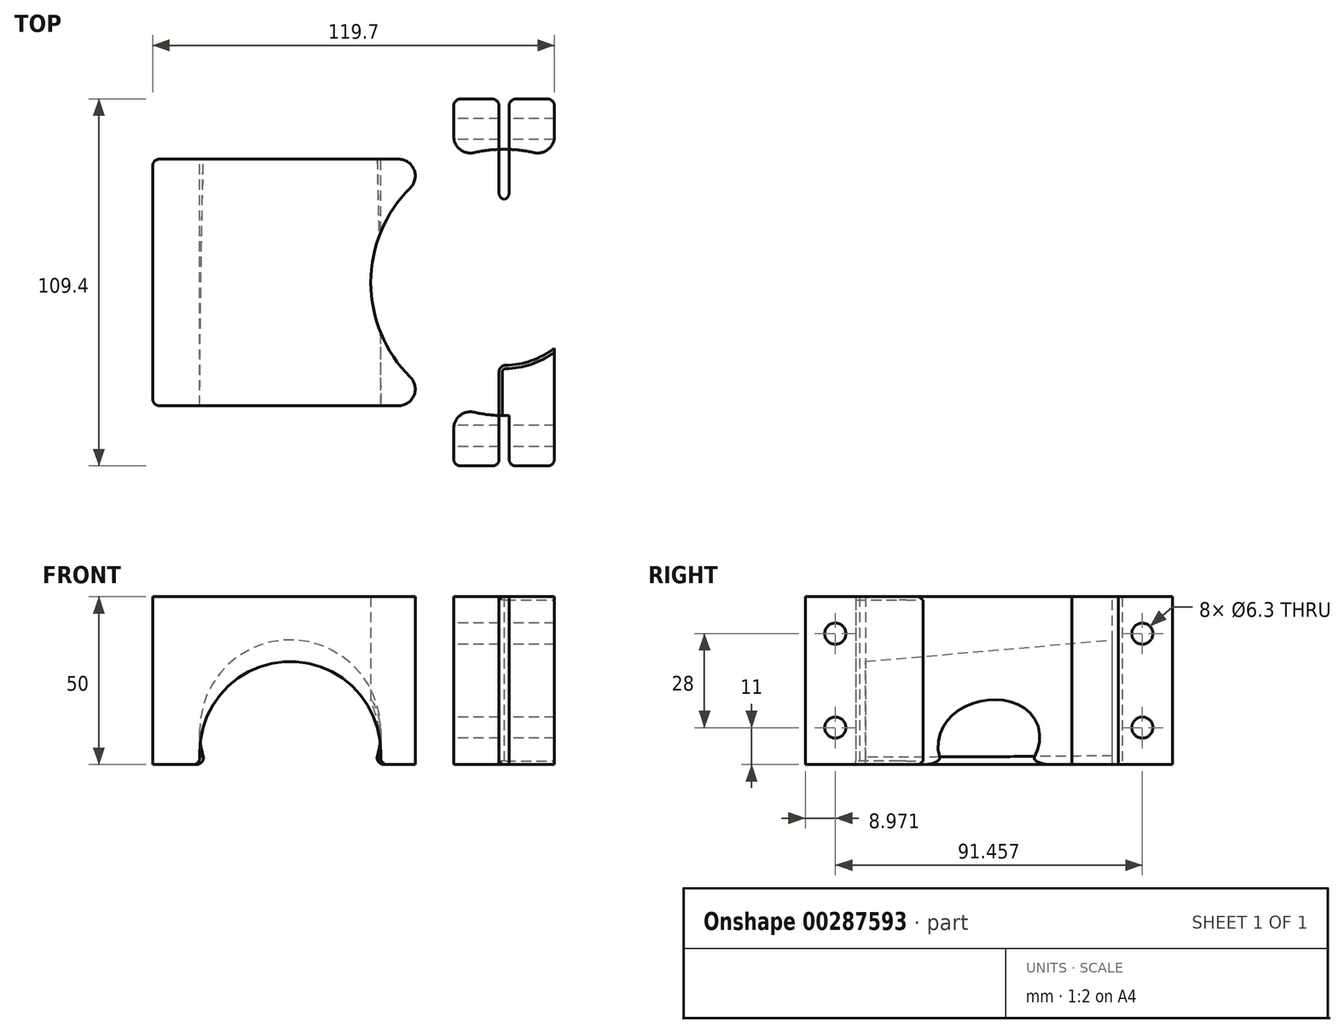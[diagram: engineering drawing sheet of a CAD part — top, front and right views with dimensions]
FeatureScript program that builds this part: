
annotation { "Feature Type Name" : "Feature", "Feature Type Description" : "" }
export const myFeature = defineFeature(function(context is Context, id is Id, definition is map)
    precondition{}
    {
        {
            var Q0;
            Q0=qCreatedBy(makeId("Top.planeOp"),FACE);
            var sketch = newSketch(context, id + "F0", { "sketchPlane" : qUnion([Q0])});
            skCircle(sketch, "E0", {"center": v(0, 0) * mm, "radius": 24.7 * mm});
            skCircle(sketch, "E1", {"center": v(0, 0) * mm, "radius": 39.7 * mm});
            skLineSegment(sketch, "E2.bottom", {"start": v(15, -54.7) * mm, "end": v(-15, -54.7) * mm});
            skLineSegment(sketch, "E2.top", {"start": v(15, 54.7) * mm, "end": v(-15, 54.7) * mm});
            skLineSegment(sketch, "E2.left", {"start": v(15, -54.7) * mm, "end": v(15, 54.7) * mm});
            skLineSegment(sketch, "E2.right", {"start": v(-15, -54.7) * mm, "end": v(-15, 54.7) * mm});
            skLineSegment(sketch, "E3.bottom", {"start": v(1.5, -54.7) * mm, "end": v(-1.5, -54.7) * mm});
            skLineSegment(sketch, "E3.top", {"start": v(1.5, 54.7) * mm, "end": v(-1.5, 54.7) * mm});
            skLineSegment(sketch, "E3.left", {"start": v(1.5, -54.7) * mm, "end": v(1.5, 54.7) * mm});
            skLineSegment(sketch, "E3.right", {"start": v(-1.5, -54.7) * mm, "end": v(-1.5, 54.7) * mm});
            skLineSegment(sketch, "E4.bottom", {"start": v(-15, 36.76) * mm, "end": v(-39.7, 36.76) * mm});
            skLineSegment(sketch, "E4.top", {"start": v(-15, -36.76) * mm, "end": v(-39.7, -36.76) * mm});
            skLineSegment(sketch, "E4.left", {"start": v(-15, 36.76) * mm, "end": v(-15, -36.76) * mm});
            skLineSegment(sketch, "E4.right", {"start": v(-39.7, 36.76) * mm, "end": v(-39.7, -36.76) * mm});
            skPoint(sketch, "E5", {"position": v(-15, -36.76) * mm});
            skSolve(sketch);
        }
        {
            var Q0;
            {var subQ0=sQuery(id+"F0.wireOp",EDGE,"E3.right");var subQ1=sQuery(id+"F0.wireOp",EDGE,"E0");var subQ2=makeQuery(id+"F0.imprint","INTERSECT",VERTEX,{"disambiguationData":[OD(0.0)],"derivedFrom":[subQ1,subQ0]});Q0=makeQuery(id+"F0.imprint","IMPRINT",FACE,{"disambiguationData":[TD([[makeQuery(id+"F0.imprint","IMPRINT",EDGE,{"disambiguationData":[TD([[subQ2,-1.0]])],"derivedFrom":subQ1}),-1.0]])]});}
            var Q1;
            {var subQ0=sQuery(id+"F0.wireOp",EDGE,"E2.right");var subQ5=sQuery(id+"F0.wireOp",EDGE,"E2.top");var subQ6=makeQuery(id+"F0.imprint","INTERSECT",VERTEX,{"derivedFrom":[subQ5,subQ0]});Q1=makeQuery(id+"F0.imprint","IMPRINT",FACE,{"disambiguationData":[TD([[makeQuery(id+"F0.imprint","IMPRINT",EDGE,{"disambiguationData":[TD([[subQ6,1.0]])],"derivedFrom":subQ5}),1.0]])]});}
            var Q2;
            {var subQ0=sQuery(id+"F0.wireOp",EDGE,"E4.left");var subQ4=sQuery(id+"F0.wireOp",EDGE,"E0");var subQ5=makeQuery(id+"F0.imprint","INTERSECT",VERTEX,{"disambiguationData":[OD(0.0)],"derivedFrom":[subQ4,subQ0]});Q2=makeQuery(id+"F0.imprint","IMPRINT",FACE,{"disambiguationData":[TD([[makeQuery(id+"F0.imprint","IMPRINT",EDGE,{"disambiguationData":[TD([[subQ5,-1.0]])],"derivedFrom":subQ4}),-1.0]])]});}
            var Q3;
            {var subQ0=sQuery(id+"F0.wireOp",EDGE,"E4.bottom");Q3=makeQuery(id+"F0.imprint","IMPRINT",FACE,{"disambiguationData":[TD([[makeQuery(id+"F0.imprint","IMPRINT",EDGE,{"derivedFrom":subQ0}),1.0]])]});}
            var Q4;
            {var subQ0=sQuery(id+"F0.wireOp",EDGE,"E4.top");Q4=makeQuery(id+"F0.imprint","IMPRINT",FACE,{"disambiguationData":[TD([[makeQuery(id+"F0.imprint","IMPRINT",EDGE,{"derivedFrom":subQ0}),-1.0]])]});}
            var Q5;
            {var subQ0=sQuery(id+"F0.wireOp",EDGE,"E4.left");var subQ1=sQuery(id+"F0.wireOp",EDGE,"E0");var subQ2=makeQuery(id+"F0.imprint","INTERSECT",VERTEX,{"disambiguationData":[OD(1.0)],"derivedFrom":[subQ1,subQ0]});Q5=makeQuery(id+"F0.imprint","IMPRINT",FACE,{"disambiguationData":[TD([[makeQuery(id+"F0.imprint","IMPRINT",EDGE,{"disambiguationData":[TD([[subQ2,-1.0]])],"derivedFrom":subQ1}),-1.0]])]});}
            var Q6;
            {var subQ0=sQuery(id+"F0.wireOp",EDGE,"E2.right");var subQ5=sQuery(id+"F0.wireOp",EDGE,"E2.bottom");var subQ6=makeQuery(id+"F0.imprint","INTERSECT",VERTEX,{"derivedFrom":[subQ5,subQ0]});Q6=makeQuery(id+"F0.imprint","IMPRINT",FACE,{"disambiguationData":[TD([[makeQuery(id+"F0.imprint","IMPRINT",EDGE,{"disambiguationData":[TD([[subQ6,1.0]])],"derivedFrom":subQ5}),-1.0]])]});}
            var Q7;
            {var subQ0=sQuery(id+"F0.wireOp",EDGE,"E2.left");var subQ1=sQuery(id+"F0.wireOp",EDGE,"E1");var subQ2=makeQuery(id+"F0.imprint","INTERSECT",VERTEX,{"disambiguationData":[OD(1.0)],"derivedFrom":[subQ1,subQ0]});Q7=makeQuery(id+"F0.imprint","IMPRINT",FACE,{"disambiguationData":[TD([[makeQuery(id+"F0.imprint","IMPRINT",EDGE,{"disambiguationData":[TD([[subQ2,1.0]])],"derivedFrom":subQ1}),-1.0]])]});}
            var Q8;
            {var subQ0=sQuery(id+"F0.wireOp",EDGE,"E3.left");var subQ1=sQuery(id+"F0.wireOp",EDGE,"E0");var subQ2=makeQuery(id+"F0.imprint","INTERSECT",VERTEX,{"disambiguationData":[OD(1.0)],"derivedFrom":[subQ1,subQ0]});Q8=makeQuery(id+"F0.imprint","IMPRINT",FACE,{"disambiguationData":[TD([[makeQuery(id+"F0.imprint","IMPRINT",EDGE,{"disambiguationData":[TD([[subQ2,-1.0]])],"derivedFrom":subQ1}),-1.0]])]});}
            var Q9;
            {var subQ0=sQuery(id+"F0.wireOp",EDGE,"E2.left");var subQ1=sQuery(id+"F0.wireOp",EDGE,"E0");var subQ2=makeQuery(id+"F0.imprint","INTERSECT",VERTEX,{"disambiguationData":[OD(0.0)],"derivedFrom":[subQ1,subQ0]});Q9=makeQuery(id+"F0.imprint","IMPRINT",FACE,{"disambiguationData":[TD([[makeQuery(id+"F0.imprint","IMPRINT",EDGE,{"disambiguationData":[TD([[subQ2,1.0]])],"derivedFrom":subQ1}),-1.0]])]});}
            var Q10;
            {var subQ0=sQuery(id+"F0.wireOp",EDGE,"E3.left");var subQ1=sQuery(id+"F0.wireOp",EDGE,"E0");var subQ2=makeQuery(id+"F0.imprint","INTERSECT",VERTEX,{"disambiguationData":[OD(0.0)],"derivedFrom":[subQ1,subQ0]});Q10=makeQuery(id+"F0.imprint","IMPRINT",FACE,{"disambiguationData":[TD([[makeQuery(id+"F0.imprint","IMPRINT",EDGE,{"disambiguationData":[TD([[subQ2,1.0]])],"derivedFrom":subQ1}),-1.0]])]});}
            var Q11;
            {var subQ0=sQuery(id+"F0.wireOp",EDGE,"E2.left");var subQ1=sQuery(id+"F0.wireOp",EDGE,"E1");var subQ2=makeQuery(id+"F0.imprint","INTERSECT",VERTEX,{"disambiguationData":[OD(0.0)],"derivedFrom":[subQ1,subQ0]});Q11=makeQuery(id+"F0.imprint","IMPRINT",FACE,{"disambiguationData":[TD([[makeQuery(id+"F0.imprint","IMPRINT",EDGE,{"disambiguationData":[TD([[subQ2,-1.0]])],"derivedFrom":subQ1}),-1.0]])]});}
            extrude(context, id + "F1", {"entities" : qUnion([Q0, Q1, Q2, Q3, Q4, Q5, Q6, Q7, Q8, Q9, Q10, Q11]), "depth" : 50 * mm, "offsetDistance" : 25 * mm});
        }
        {
            var Q0;
            Q0=makeQuery(id+"F1.opExtrude","SWEPT_FACE",FACE,{"disambiguationData":[OSD([sQuery(id+"F0.wireOp",EDGE,"E4.right")])]});
            extrude(context, id + "F2", {"entities" : qUnion([Q0]), "operationType" : NewBodyOperationType.ADD, "depth" : 65 * mm, "offsetDistance" : 25 * mm});
        }
        {
            var Q0;
            {var subQ0=sQuery(id+"F0.wireOp",EDGE,"E4.right");var subQ1=sQuery(id+"F0.wireOp",EDGE,"E4.bottom");Q0=makeQuery(id+"F2.boolean.opBoolean","MERGE",EDGE,{"derivedFrom":[makeQuery(id+"F1.opExtrude","CAP_EDGE",EDGE,{"disambiguationData":[OSD([subQ1])],"isStart":true}),makeQuery(id+"F2.opExtrude","SWEPT_EDGE",EDGE,{"disambiguationData":[OSD([subQ1,subQ0]),TDD([makeQuery(id+"F1.opExtrude","CAP_VERTEX",VERTEX,{"disambiguationData":[OSD([subQ1,subQ0])],"isStart":true})])]})]});}
            cPlane(context, id + "F3", {"entities" : qUnion([Q0]), "cplaneType" : CPlaneType.LINE_ANGLE, "offset" : 25 * mm, "angle" : 5 * degree, "oppositeDirection" : true, "width" : 150 * mm, "height" : 150 * mm});
        }
        {
            var Q0;
            Q0=qCreatedBy(id+"F3.planeOp",FACE);
            var sketch = newSketch(context, id + "F4", { "sketchPlane" : qUnion([Q0])});
            skCircle(sketch, "E6", {"center": v(-63.7, 6.8) * mm, "radius": 27 * mm});
            skSolve(sketch);
        }
        {
            var Q0;
            Q0=makeQuery(id+"F4.imprint","IMPRINT",FACE,{"disambiguationData":[TD([[makeQuery(id+"F4.imprint","IMPRINT",EDGE,{"derivedFrom":sQuery(id+"F4.wireOp",EDGE,"E6")}),1.0]])]});
            extrude(context, id + "F5", {"entities" : qUnion([Q0]), "operationType" : NewBodyOperationType.REMOVE, "endBound" : BoundingType.THROUGH_ALL, "depth" : 25 * mm, "offsetDistance" : 25 * mm, "hasSecondDirection" : true, "secondDirectionBound" : BoundingType.THROUGH_ALL, "secondDirectionOppositeDirection" : true, "secondDirectionDepth" : 25 * mm});
        }
        {
            var Q0;
            {var subQ0=sQuery(id+"F0.wireOp",EDGE,"E2.right");Q0=makeQuery(id+"F1.opExtrude","SWEPT_FACE",FACE,{"disambiguationData":[OSD([subQ0]),TDD([makeQuery(id+"F0.imprint","IMPRINT",EDGE,{"disambiguationData":[TD([[makeQuery(id+"F0.imprint","INTERSECT",VERTEX,{"derivedFrom":[sQuery(id+"F0.wireOp",EDGE,"E2.top"),subQ0]}),1.0]])],"derivedFrom":subQ0})])]});}
            var sketch = newSketch(context, id + "F6", { "sketchPlane" : qUnion([Q0])});
            skLineSegment(sketch, "E7", {"start": v(-54.7, 25) * mm, "end": v(-36.76, 25) * mm, "construction": true});
            skPoint(sketch, "E8", {"position": v(-45.73, 0) * mm});
            skCircle(sketch, "E9", {"center": v(-45.73, 11) * mm, "radius": 3.15 * mm});
            skCircle(sketch, "E10.MirrorC", {"center": v(-45.73, 39) * mm, "radius": 3.15 * mm});
            skCircle(sketch, "E11.MirrorC", {"center": v(45.73, 39) * mm, "radius": 3.15 * mm});
            skCircle(sketch, "E12.MirrorC", {"center": v(45.73, 11) * mm, "radius": 3.15 * mm});
            skSolve(sketch);
        }
        {
            var Q0;
            Q0 = qSketchRegion(id + "F6", true);
            extrude(context, id + "F7", {"entities" : qUnion([Q0]), "operationType" : NewBodyOperationType.REMOVE, "endBound" : BoundingType.THROUGH_ALL, "oppositeDirection" : true, "depth" : 25 * mm, "offsetDistance" : 25 * mm});
        }
        {
            var Q0;
            Q0=makeQuery(id+"F1.opExtrude","SWEPT_EDGE",EDGE,{"disambiguationData":[OSD([sQuery(id+"F0.wireOp",EDGE,"E2.top"),sQuery(id+"F0.wireOp",EDGE,"E2.left")])]});
            var Q1;
            Q1=makeQuery(id+"F1.opExtrude","SWEPT_EDGE",EDGE,{"disambiguationData":[OSD([sQuery(id+"F0.wireOp",EDGE,"E2.top"),sQuery(id+"F0.wireOp",EDGE,"E3.top"),sQuery(id+"F0.wireOp",EDGE,"E3.left")])]});
            var Q2;
            Q2=makeQuery(id+"F1.opExtrude","SWEPT_EDGE",EDGE,{"disambiguationData":[OSD([sQuery(id+"F0.wireOp",EDGE,"E2.top"),sQuery(id+"F0.wireOp",EDGE,"E3.top"),sQuery(id+"F0.wireOp",EDGE,"E3.right")])]});
            var Q3;
            Q3=makeQuery(id+"F1.opExtrude","SWEPT_EDGE",EDGE,{"disambiguationData":[OSD([sQuery(id+"F0.wireOp",EDGE,"E2.top"),sQuery(id+"F0.wireOp",EDGE,"E2.right")])]});
            var Q4;
            Q4=makeQuery(id+"F1.opExtrude","SWEPT_EDGE",EDGE,{"disambiguationData":[OSD([sQuery(id+"F0.wireOp",EDGE,"E2.bottom"),sQuery(id+"F0.wireOp",EDGE,"E2.right")])]});
            var Q5;
            Q5=makeQuery(id+"F1.opExtrude","SWEPT_EDGE",EDGE,{"disambiguationData":[OSD([sQuery(id+"F0.wireOp",EDGE,"E2.bottom"),sQuery(id+"F0.wireOp",EDGE,"E3.bottom"),sQuery(id+"F0.wireOp",EDGE,"E3.right")])]});
            var Q6;
            Q6=makeQuery(id+"F1.opExtrude","SWEPT_EDGE",EDGE,{"disambiguationData":[OSD([sQuery(id+"F0.wireOp",EDGE,"E2.bottom"),sQuery(id+"F0.wireOp",EDGE,"E2.left")])]});
            var Q7;
            Q7=makeQuery(id+"F1.opExtrude","SWEPT_EDGE",EDGE,{"disambiguationData":[OSD([sQuery(id+"F0.wireOp",EDGE,"E2.bottom"),sQuery(id+"F0.wireOp",EDGE,"E3.bottom"),sQuery(id+"F0.wireOp",EDGE,"E3.left")])]});
            var Q8;
            Q8=makeQuery(id+"F2.opExtrude","CAP_EDGE",EDGE,{"disambiguationData":[OSD([sQuery(id+"F0.wireOp",EDGE,"E4.bottom"),sQuery(id+"F0.wireOp",EDGE,"E4.right")])],"isStart":false});
            var Q9;
            Q9=makeQuery(id+"F2.opExtrude","CAP_EDGE",EDGE,{"disambiguationData":[OSD([sQuery(id+"F0.wireOp",EDGE,"E4.top"),sQuery(id+"F0.wireOp",EDGE,"E4.right")])],"isStart":false});
            var Q10;
            {var subQ0=sQuery(id+"F0.wireOp",EDGE,"E4.right");Q10=makeQuery(id+"F5.boolean.opBoolean","INTERSECT",EDGE,{"disambiguationData":[OD(1.0)],"derivedFrom":[makeQuery(id+"F2.boolean.opBoolean","MERGE",FACE,{"derivedFrom":[makeQuery(id+"F1.opExtrude","CAP_FACE",FACE,{"disambiguationData":[OSD([sQuery(id+"F0.wireOp",EDGE,"E0"),sQuery(id+"F0.wireOp",EDGE,"E2.bottom"),sQuery(id+"F0.wireOp",EDGE,"E2.top"),sQuery(id+"F0.wireOp",EDGE,"E2.right"),sQuery(id+"F0.wireOp",EDGE,"E3.right"),sQuery(id+"F0.wireOp",EDGE,"E4.bottom"),sQuery(id+"F0.wireOp",EDGE,"E4.top"),subQ0])],"isStart":true}),makeQuery(id+"F2.opExtrude","SWEPT_FACE",FACE,{"disambiguationData":[OSD([subQ0]),TDD([makeQuery(id+"F1.opExtrude","CAP_EDGE",EDGE,{"disambiguationData":[OSD([subQ0])],"isStart":true})])]})]}),makeQuery(id+"F5.opExtrude","SWEPT_FACE",FACE,{"disambiguationData":[OSD([sQuery(id+"F4.wireOp",EDGE,"E6")])]})]});}
            var Q11;
            {var subQ0=sQuery(id+"F0.wireOp",EDGE,"E4.right");Q11=makeQuery(id+"F5.boolean.opBoolean","INTERSECT",EDGE,{"disambiguationData":[OD(0.0)],"derivedFrom":[makeQuery(id+"F2.boolean.opBoolean","MERGE",FACE,{"derivedFrom":[makeQuery(id+"F1.opExtrude","CAP_FACE",FACE,{"disambiguationData":[OSD([sQuery(id+"F0.wireOp",EDGE,"E0"),sQuery(id+"F0.wireOp",EDGE,"E2.bottom"),sQuery(id+"F0.wireOp",EDGE,"E2.top"),sQuery(id+"F0.wireOp",EDGE,"E2.right"),sQuery(id+"F0.wireOp",EDGE,"E3.right"),sQuery(id+"F0.wireOp",EDGE,"E4.bottom"),sQuery(id+"F0.wireOp",EDGE,"E4.top"),subQ0])],"isStart":true}),makeQuery(id+"F2.opExtrude","SWEPT_FACE",FACE,{"disambiguationData":[OSD([subQ0]),TDD([makeQuery(id+"F1.opExtrude","CAP_EDGE",EDGE,{"disambiguationData":[OSD([subQ0])],"isStart":true})])]})]}),makeQuery(id+"F5.opExtrude","SWEPT_FACE",FACE,{"disambiguationData":[OSD([sQuery(id+"F4.wireOp",EDGE,"E6")])]})]});}
            fillet(context, id + "F8", {"entities" : qUnion([Q0, Q1, Q2, Q3, Q4, Q5, Q6, Q7, Q8, Q9, Q10, Q11]), "tangentPropagation" : true, "radius" : 2 * mm, "defaultsChanged" : false, "vertexSettings" : [], "allowEdgeOverflow" : false});
        }
        {
            var Q0;
            Q0=makeQuery(id+"F1.opExtrude","SWEPT_EDGE",EDGE,{"disambiguationData":[OSD([sQuery(id+"F0.wireOp",EDGE,"E1"),sQuery(id+"F0.wireOp",EDGE,"E2.right"),sQuery(id+"F0.wireOp",EDGE,"E4.top"),sQuery(id+"F0.wireOp",EDGE,"E4.left")])]});
            var Q1;
            {var subQ0=sQuery(id+"F0.wireOp",EDGE,"E2.left");var subQ1=sQuery(id+"F0.wireOp",EDGE,"E1");Q1=makeQuery(id+"F1.opExtrude","SWEPT_EDGE",EDGE,{"disambiguationData":[OSD([subQ1,subQ0]),TDD([makeQuery(id+"F0.imprint","INTERSECT",VERTEX,{"disambiguationData":[OD(1.0)],"derivedFrom":[subQ1,subQ0]})])]});}
            var Q2;
            Q2=makeQuery(id+"F1.opExtrude","SWEPT_EDGE",EDGE,{"disambiguationData":[OSD([sQuery(id+"F0.wireOp",EDGE,"E1"),sQuery(id+"F0.wireOp",EDGE,"E2.right"),sQuery(id+"F0.wireOp",EDGE,"E4.bottom"),sQuery(id+"F0.wireOp",EDGE,"E4.left")])]});
            var Q3;
            {var subQ0=sQuery(id+"F0.wireOp",EDGE,"E2.left");var subQ1=sQuery(id+"F0.wireOp",EDGE,"E1");Q3=makeQuery(id+"F1.opExtrude","SWEPT_EDGE",EDGE,{"disambiguationData":[OSD([subQ1,subQ0]),TDD([makeQuery(id+"F0.imprint","INTERSECT",VERTEX,{"disambiguationData":[OD(0.0)],"derivedFrom":[subQ1,subQ0]})])]});}
            fillet(context, id + "F9", {"entities" : qUnion([Q0, Q1, Q2, Q3]), "tangentPropagation" : true, "radius" : 5 * mm, "defaultsChanged" : false, "vertexSettings" : [], "allowEdgeOverflow" : false});
        }
        {
            var Q0;
            {var subQ0=sQuery(id+"F0.wireOp",EDGE,"E3.right");var subQ1=sQuery(id+"F0.wireOp",EDGE,"E0");Q0=makeQuery(id+"F1.opExtrude","SWEPT_EDGE",EDGE,{"disambiguationData":[OSD([subQ1,subQ0]),TDD([makeQuery(id+"F0.imprint","INTERSECT",VERTEX,{"disambiguationData":[OD(0.0)],"derivedFrom":[subQ1,subQ0]})])]});}
            var Q1;
            {var subQ0=sQuery(id+"F0.wireOp",EDGE,"E3.left");var subQ1=sQuery(id+"F0.wireOp",EDGE,"E0");Q1=makeQuery(id+"F1.opExtrude","SWEPT_EDGE",EDGE,{"disambiguationData":[OSD([subQ1,subQ0]),TDD([makeQuery(id+"F0.imprint","INTERSECT",VERTEX,{"disambiguationData":[OD(0.0)],"derivedFrom":[subQ1,subQ0]})])]});}
            var Q2;
            {var subQ0=sQuery(id+"F0.wireOp",EDGE,"E3.left");var subQ1=sQuery(id+"F0.wireOp",EDGE,"E0");Q2=makeQuery(id+"F1.opExtrude","SWEPT_EDGE",EDGE,{"disambiguationData":[OSD([subQ1,subQ0]),TDD([makeQuery(id+"F0.imprint","INTERSECT",VERTEX,{"disambiguationData":[OD(1.0)],"derivedFrom":[subQ1,subQ0]})])]});}
            var Q3;
            {var subQ0=sQuery(id+"F0.wireOp",EDGE,"E3.right");var subQ1=sQuery(id+"F0.wireOp",EDGE,"E0");Q3=makeQuery(id+"F1.opExtrude","SWEPT_EDGE",EDGE,{"disambiguationData":[OSD([subQ1,subQ0]),TDD([makeQuery(id+"F0.imprint","INTERSECT",VERTEX,{"disambiguationData":[OD(1.0)],"derivedFrom":[subQ1,subQ0]})])]});}
            fillet(context, id + "F10", {"entities" : qUnion([Q0, Q1, Q2, Q3]), "tangentPropagation" : true, "radius" : 2 * mm, "defaultsChanged" : false, "vertexSettings" : [], "allowEdgeOverflow" : false});
        }
        {
            var Q0;
            {var subQ0=sQuery(id+"F0.wireOp",EDGE,"E4.left");var subQ1=sQuery(id+"F0.wireOp",EDGE,"E0");var subQ2=makeQuery(id+"F0.imprint","INTERSECT",VERTEX,{"disambiguationData":[OD(1.0)],"derivedFrom":[subQ1,subQ0]});var subQ3=sQuery(id+"F0.wireOp",EDGE,"E3.right");var subQ4=makeQuery(id+"F0.imprint","INTERSECT",VERTEX,{"disambiguationData":[OD(0.0)],"derivedFrom":[subQ1,subQ0]});Q0=makeQuery(id+"F1.opExtrude","CAP_EDGE",EDGE,{"disambiguationData":[OSD([subQ1]),TDD([makeQuery(id+"F0.imprint","IMPRINT",EDGE,{"disambiguationData":[TD([[makeQuery(id+"F0.imprint","INTERSECT",VERTEX,{"disambiguationData":[OD(0.0)],"derivedFrom":[subQ1,subQ3]}),-1.0]])],"derivedFrom":subQ1}),makeQuery(id+"F0.imprint","IMPRINT",EDGE,{"disambiguationData":[TD([[subQ4,-1.0]])],"derivedFrom":subQ1}),makeQuery(id+"F0.imprint","IMPRINT",EDGE,{"disambiguationData":[TD([[subQ2,-1.0]])],"derivedFrom":subQ1})])],"isStart":true});}
            var Q1;
            {var subQ0=sQuery(id+"F0.wireOp",EDGE,"E2.left");var subQ1=sQuery(id+"F0.wireOp",EDGE,"E0");var subQ2=makeQuery(id+"F0.imprint","INTERSECT",VERTEX,{"disambiguationData":[OD(0.0)],"derivedFrom":[subQ1,subQ0]});var subQ4=sQuery(id+"F0.wireOp",EDGE,"E3.left");Q1=makeQuery(id+"F1.opExtrude","CAP_EDGE",EDGE,{"disambiguationData":[OSD([subQ1]),TDD([makeQuery(id+"F0.imprint","IMPRINT",EDGE,{"disambiguationData":[TD([[makeQuery(id+"F0.imprint","INTERSECT",VERTEX,{"disambiguationData":[OD(0.0)],"derivedFrom":[subQ1,subQ4]}),1.0]])],"derivedFrom":subQ1}),makeQuery(id+"F0.imprint","IMPRINT",EDGE,{"disambiguationData":[TD([[makeQuery(id+"F0.imprint","INTERSECT",VERTEX,{"disambiguationData":[OD(1.0)],"derivedFrom":[subQ1,subQ4]}),-1.0]])],"derivedFrom":subQ1}),makeQuery(id+"F0.imprint","IMPRINT",EDGE,{"disambiguationData":[TD([[subQ2,1.0]])],"derivedFrom":subQ1})])],"isStart":true});}
            var Q2;
            {var subQ0=sQuery(id+"F0.wireOp",EDGE,"E2.left");var subQ1=sQuery(id+"F0.wireOp",EDGE,"E0");var subQ2=makeQuery(id+"F0.imprint","INTERSECT",VERTEX,{"disambiguationData":[OD(0.0)],"derivedFrom":[subQ1,subQ0]});var subQ4=sQuery(id+"F0.wireOp",EDGE,"E3.left");Q2=makeQuery(id+"F1.opExtrude","CAP_EDGE",EDGE,{"disambiguationData":[OSD([subQ1]),TDD([makeQuery(id+"F0.imprint","IMPRINT",EDGE,{"disambiguationData":[TD([[makeQuery(id+"F0.imprint","INTERSECT",VERTEX,{"disambiguationData":[OD(0.0)],"derivedFrom":[subQ1,subQ4]}),1.0]])],"derivedFrom":subQ1}),makeQuery(id+"F0.imprint","IMPRINT",EDGE,{"disambiguationData":[TD([[makeQuery(id+"F0.imprint","INTERSECT",VERTEX,{"disambiguationData":[OD(1.0)],"derivedFrom":[subQ1,subQ4]}),-1.0]])],"derivedFrom":subQ1}),makeQuery(id+"F0.imprint","IMPRINT",EDGE,{"disambiguationData":[TD([[subQ2,1.0]])],"derivedFrom":subQ1})])],"isStart":false});}
            var Q3;
            {var subQ0=sQuery(id+"F0.wireOp",EDGE,"E4.left");var subQ1=sQuery(id+"F0.wireOp",EDGE,"E0");var subQ2=makeQuery(id+"F0.imprint","INTERSECT",VERTEX,{"disambiguationData":[OD(1.0)],"derivedFrom":[subQ1,subQ0]});var subQ3=sQuery(id+"F0.wireOp",EDGE,"E3.right");var subQ4=makeQuery(id+"F0.imprint","INTERSECT",VERTEX,{"disambiguationData":[OD(0.0)],"derivedFrom":[subQ1,subQ0]});Q3=makeQuery(id+"F1.opExtrude","CAP_EDGE",EDGE,{"disambiguationData":[OSD([subQ1]),TDD([makeQuery(id+"F0.imprint","IMPRINT",EDGE,{"disambiguationData":[TD([[makeQuery(id+"F0.imprint","INTERSECT",VERTEX,{"disambiguationData":[OD(0.0)],"derivedFrom":[subQ1,subQ3]}),-1.0]])],"derivedFrom":subQ1}),makeQuery(id+"F0.imprint","IMPRINT",EDGE,{"disambiguationData":[TD([[subQ4,-1.0]])],"derivedFrom":subQ1}),makeQuery(id+"F0.imprint","IMPRINT",EDGE,{"disambiguationData":[TD([[subQ2,-1.0]])],"derivedFrom":subQ1})])],"isStart":false});}
            chamfer(context, id + "F11", {"entities" : qUnion([Q0, Q1, Q2, Q3]), "width" : 1 * mm, "tangentPropagation" : true});
        }
    });
